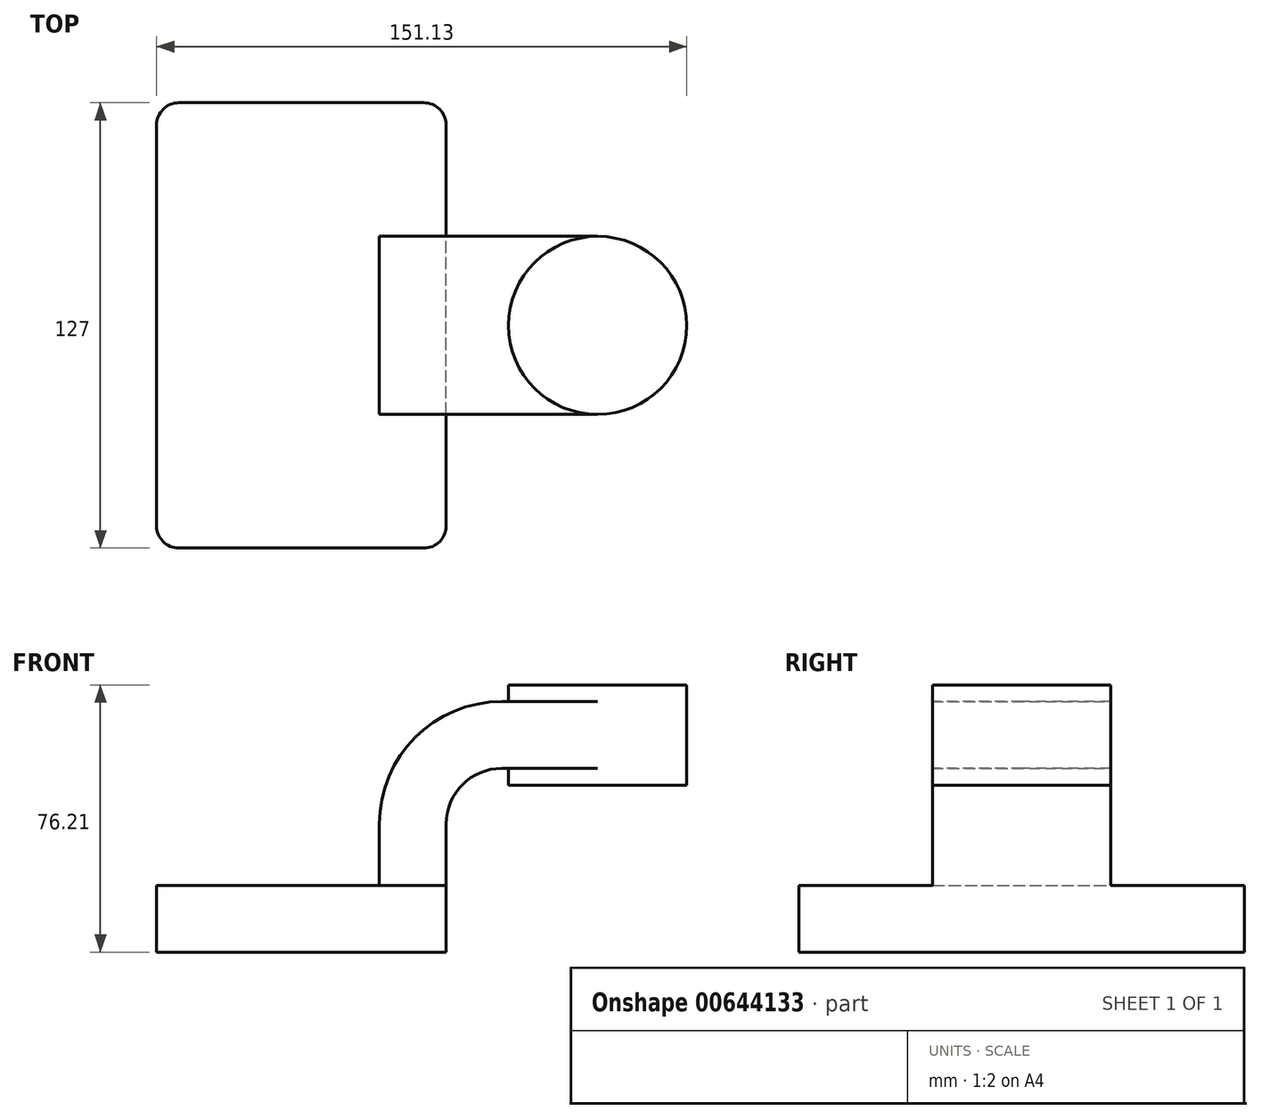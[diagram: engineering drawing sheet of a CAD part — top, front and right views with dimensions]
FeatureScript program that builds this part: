
annotation { "Feature Type Name" : "Feature", "Feature Type Description" : "" }
export const myFeature = defineFeature(function(context is Context, id is Id, definition is map)
    precondition{}
    {
        {
            var Q0;
            Q0=qCreatedBy(makeId("Front.planeOp"),FACE);
            var sketch = newSketch(context, id + "F0", { "sketchPlane" : qUnion([Q0])});
            skLineSegment(sketch, "E0.bottom", {"start": v(41.27, 9.53) * mm, "end": v(-41.27, 9.53) * mm});
            skLineSegment(sketch, "E0.top", {"start": v(41.27, -9.52) * mm, "end": v(-41.27, -9.53) * mm});
            skLineSegment(sketch, "E0.left", {"start": v(41.27, 9.53) * mm, "end": v(41.27, -9.52) * mm});
            skLineSegment(sketch, "E0.right", {"start": v(-41.27, 9.53) * mm, "end": v(-41.27, -9.52) * mm});
            skPoint(sketch, "E0.middle", {"position": v(0, 0) * mm});
            skLineSegment(sketch, "E1.bottom", {"start": v(109.86, 38.1) * mm, "end": v(59.05, 38.1) * mm});
            skLineSegment(sketch, "E1.top", {"start": v(109.86, 66.68) * mm, "end": v(59.05, 66.68) * mm});
            skLineSegment(sketch, "E1.left", {"start": v(109.86, 38.1) * mm, "end": v(109.86, 66.68) * mm});
            skLineSegment(sketch, "E1.right", {"start": v(59.05, 38.1) * mm, "end": v(59.05, 66.68) * mm});
            skPoint(sketch, "E1.middle", {"position": v(84.45, 52.39) * mm});
            skLineSegment(sketch, "E2", {"start": v(41.27, 9.53) * mm, "end": v(41.27, 27) * mm});
            skArc(sketch, "E3", {"start": v(41.28, 27) * mm, "mid": v(45.92, 38.23) * mm, "end": v(57.15, 42.88) * mm});
            skLineSegment(sketch, "E4", {"start": v(57.15, 42.88) * mm, "end": v(84.45, 42.88) * mm});
            skLineSegment(sketch, "E5.0", {"start": v(57.15, 61.93) * mm, "end": v(84.45, 61.93) * mm});
            skArc(sketch, "E5.1", {"start": v(22.23, 27) * mm, "mid": v(32.45, 51.7) * mm, "end": v(57.15, 61.93) * mm});
            skLineSegment(sketch, "E5.2", {"start": v(22.23, 9.53) * mm, "end": v(22.23, 27) * mm});
            skLineSegment(sketch, "E6", {"start": v(84.45, 38.1) * mm, "end": v(84.45, 66.68) * mm});
            skFitSpline(sketch, "E7", {"points": [v(-41.28, 9.53) * mm, v(57.15, 61.93) * mm], "startDerivative": vector(0, 86.13) * mm, "endDerivative": vector(111.29, 0) * mm});
            skSolve(sketch);
        }
        {
            var Q0;
            Q0=makeQuery(id+"F0.imprint","IMPRINT",FACE,{"disambiguationData":[TD([[makeQuery(id+"F0.imprint","IMPRINT",EDGE,{"derivedFrom":sQuery(id+"F0.wireOp",EDGE,"E0.top")}),-1.0]])]});
            extrude(context, id + "F1", {"entities" : qUnion([Q0]), "endBound" : BoundingType.SYMMETRIC, "depth" : 127 * mm, "offsetDistance" : 25.4 * mm});
        }
        {
            var Q0;
            {var subQ1=sQuery(id+"F0.wireOp",EDGE,"E2");Q0=makeQuery(id+"F0.imprint","IMPRINT",FACE,{"disambiguationData":[TD([[makeQuery(id+"F0.imprint","IMPRINT",EDGE,{"derivedFrom":subQ1}),1.0]])]});}
            var Q1;
            {var subQ0=sQuery(id+"F0.wireOp",EDGE,"E4");var subQ1=sQuery(id+"F0.wireOp",EDGE,"E1.right");var subQ2=makeQuery(id+"F0.imprint","INTERSECT",VERTEX,{"derivedFrom":[subQ1,subQ0]});Q1=makeQuery(id+"F0.imprint","IMPRINT",FACE,{"disambiguationData":[TD([[makeQuery(id+"F0.imprint","IMPRINT",EDGE,{"disambiguationData":[TD([[subQ2,-1.0]])],"derivedFrom":subQ1}),-1.0]])]});}
            extrude(context, id + "F2", {"entities" : qUnion([Q0, Q1]), "operationType" : NewBodyOperationType.ADD, "endBound" : BoundingType.SYMMETRIC, "depth" : 50.8 * mm, "offsetDistance" : 25.4 * mm});
        }
        {
            var Q0;
            Q0=makeQuery(id+"F0.imprint","IMPRINT",FACE,{"disambiguationData":[TD([[makeQuery(id+"F0.imprint","IMPRINT",EDGE,{"derivedFrom":sQuery(id+"F0.wireOp",EDGE,"E5.1")}),1.0]])]});
            extrude(context, id + "F3", {"entities" : qUnion([Q0]), "operationType" : NewBodyOperationType.ADD, "endBound" : BoundingType.SYMMETRIC, "depth" : 15.88 * mm, "offsetDistance" : 25.4 * mm});
        }
        {
            var Q0;
            {var subQ4=sQuery(id+"F0.wireOp",EDGE,"E1.left");Q0=makeQuery(id+"F0.imprint","IMPRINT",FACE,{"disambiguationData":[TD([[makeQuery(id+"F0.imprint","IMPRINT",EDGE,{"derivedFrom":subQ4}),1.0]])]});}
            var Q1;
            Q1=sQuery(id+"F0.wireOp",EDGE,"E6");
            revolve(context, id + "F4", {"operationType" : NewBodyOperationType.ADD, "entities" : qUnion([Q0]), "axis" : qUnion([Q1]), "revolveType" : RevolveType.SYMMETRIC, "angle" : 360 * degree});
        }
        {
            var Q0;
            Q0=makeQuery(id+"F1.opExtrude","CAP_EDGE",EDGE,{"disambiguationData":[OSD([sQuery(id+"F0.wireOp",EDGE,"E0.left")])],"isStart":false});
            var Q1;
            Q1=makeQuery(id+"F1.opExtrude","CAP_EDGE",EDGE,{"disambiguationData":[OSD([sQuery(id+"F0.wireOp",EDGE,"E0.right")])],"isStart":false});
            var Q2;
            Q2=makeQuery(id+"F1.opExtrude","CAP_EDGE",EDGE,{"disambiguationData":[OSD([sQuery(id+"F0.wireOp",EDGE,"E0.left")])],"isStart":true});
            var Q3;
            Q3=makeQuery(id+"F1.opExtrude","CAP_EDGE",EDGE,{"disambiguationData":[OSD([sQuery(id+"F0.wireOp",EDGE,"E0.right")])],"isStart":true});
            fillet(context, id + "F5", {"entities" : qUnion([Q0, Q1, Q2, Q3]), "radius" : 6.35 * mm, "tangentPropagation" : true, "allowEdgeOverflow" : false});
        }
    });
